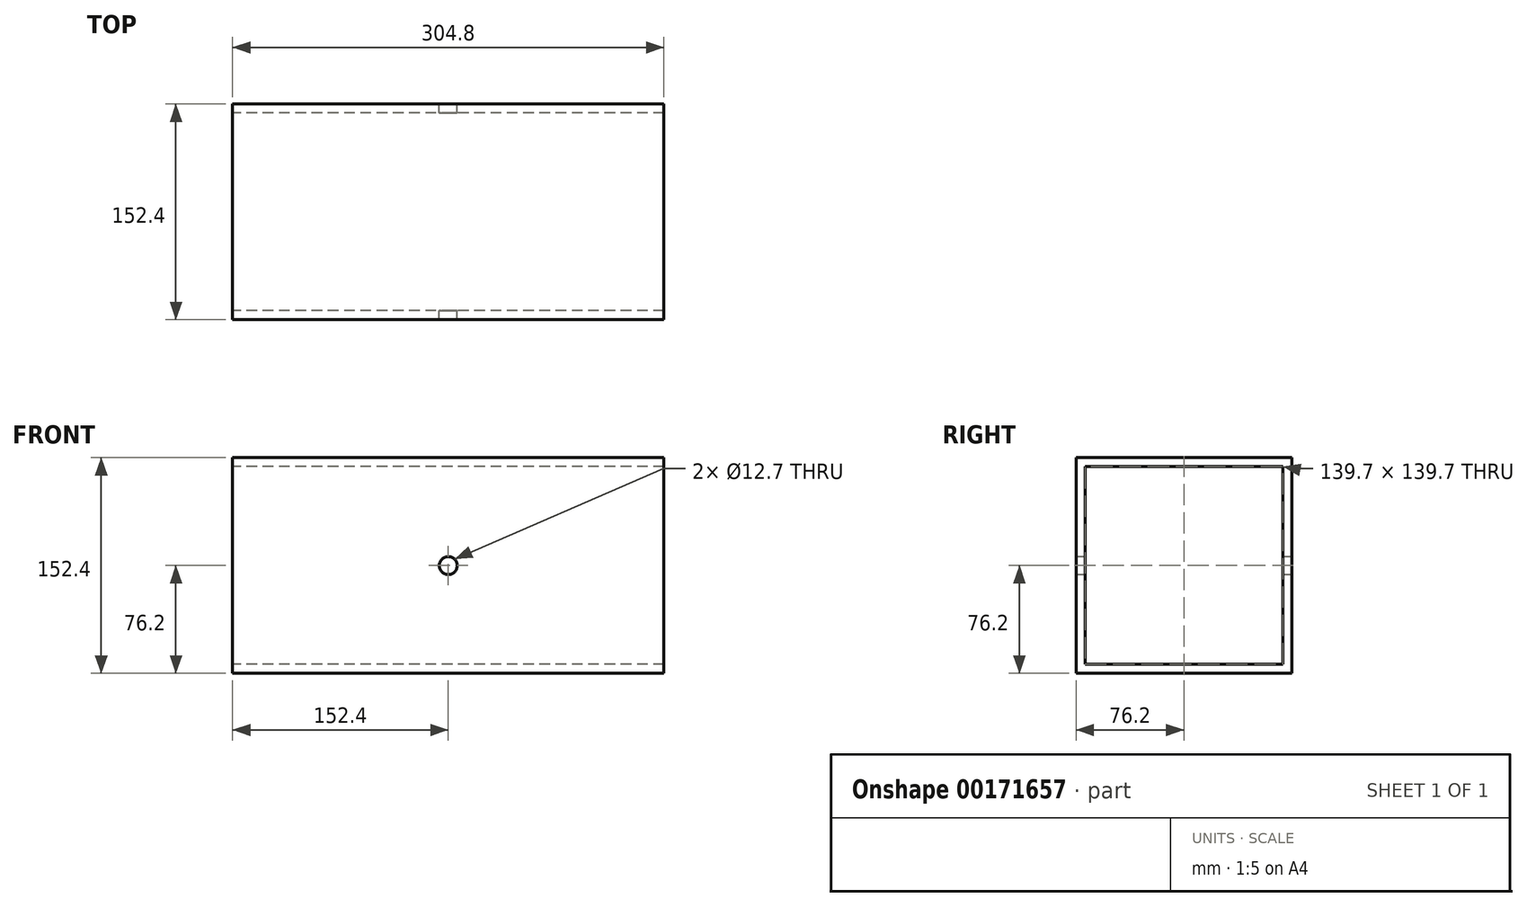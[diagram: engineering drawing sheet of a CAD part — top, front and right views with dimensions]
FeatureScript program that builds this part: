
annotation { "Feature Type Name" : "Feature", "Feature Type Description" : "" }
export const myFeature = defineFeature(function(context is Context, id is Id, definition is map)
    precondition{}
    {
        {
            var Q0;
            Q0=qCreatedBy(makeId("Right.planeOp"),FACE);
            var sketch = newSketch(context, id + "F0", { "sketchPlane" : qUnion([Q0])});
            skLineSegment(sketch, "E0.bottom", {"start": v(-76.2, 76.2) * mm, "end": v(76.2, 76.2) * mm});
            skLineSegment(sketch, "E0.top", {"start": v(-76.2, -76.2) * mm, "end": v(76.2, -76.2) * mm});
            skLineSegment(sketch, "E0.left", {"start": v(-76.2, 76.2) * mm, "end": v(-76.2, -76.2) * mm});
            skLineSegment(sketch, "E0.right", {"start": v(76.2, 76.2) * mm, "end": v(76.2, -76.2) * mm});
            skLineSegment(sketch, "E1.bottom", {"start": v(-69.85, 69.85) * mm, "end": v(69.85, 69.85) * mm});
            skLineSegment(sketch, "E1.top", {"start": v(-69.85, -69.85) * mm, "end": v(69.85, -69.85) * mm});
            skLineSegment(sketch, "E1.left", {"start": v(-69.85, 69.85) * mm, "end": v(-69.85, -69.85) * mm});
            skLineSegment(sketch, "E1.right", {"start": v(69.85, 69.85) * mm, "end": v(69.85, -69.85) * mm});
            skSolve(sketch);
        }
        {
            var Q0;
            Q0=makeQuery(id+"F0.imprint","IMPRINT",FACE,{"disambiguationData":[TD([[makeQuery(id+"F0.imprint","IMPRINT",EDGE,{"derivedFrom":sQuery(id+"F0.wireOp",EDGE,"E0.bottom")}),-1.0]])]});
            extrude(context, id + "F1", {"entities" : qUnion([Q0]), "depth" : 304.8 * mm});
        }
        {
            var Q0;
            Q0=makeQuery(id+"F1.opExtrude","SWEPT_FACE",FACE,{"disambiguationData":[OSD([sQuery(id+"F0.wireOp",EDGE,"E0.left")])]});
            var sketch = newSketch(context, id + "F2", { "sketchPlane" : qUnion([Q0])});
            skPoint(sketch, "E2", {"position": v(152.4, 0) * mm});
            skSolve(sketch);
        }
        {
            var Q0;
            Q0=sQuery(id+"F2.wireOp",VERTEX,"E2");
            var Q1;
            Q1=makeQuery(id+"F1.opExtrude","SWEPT_BODY",BODY,{"disambiguationData":[OSD([sQuery(id+"F0.wireOp",EDGE,"E0.bottom"),sQuery(id+"F0.wireOp",EDGE,"E0.top"),sQuery(id+"F0.wireOp",EDGE,"E0.left"),sQuery(id+"F0.wireOp",EDGE,"E0.right"),sQuery(id+"F0.wireOp",EDGE,"E1.bottom"),sQuery(id+"F0.wireOp",EDGE,"E1.top"),sQuery(id+"F0.wireOp",EDGE,"E1.left"),sQuery(id+"F0.wireOp",EDGE,"E1.right")])]});
            hole(context, id + "F3", {"style" : HoleStyle.SIMPLE, "endStyle" : HoleEndStyle.THROUGH, "holeDiameter" : 12.7 * mm, "locations" : qUnion([Q0]), "scope" : qUnion([Q1]), "isTappedThrough" : true});
        }
    });
